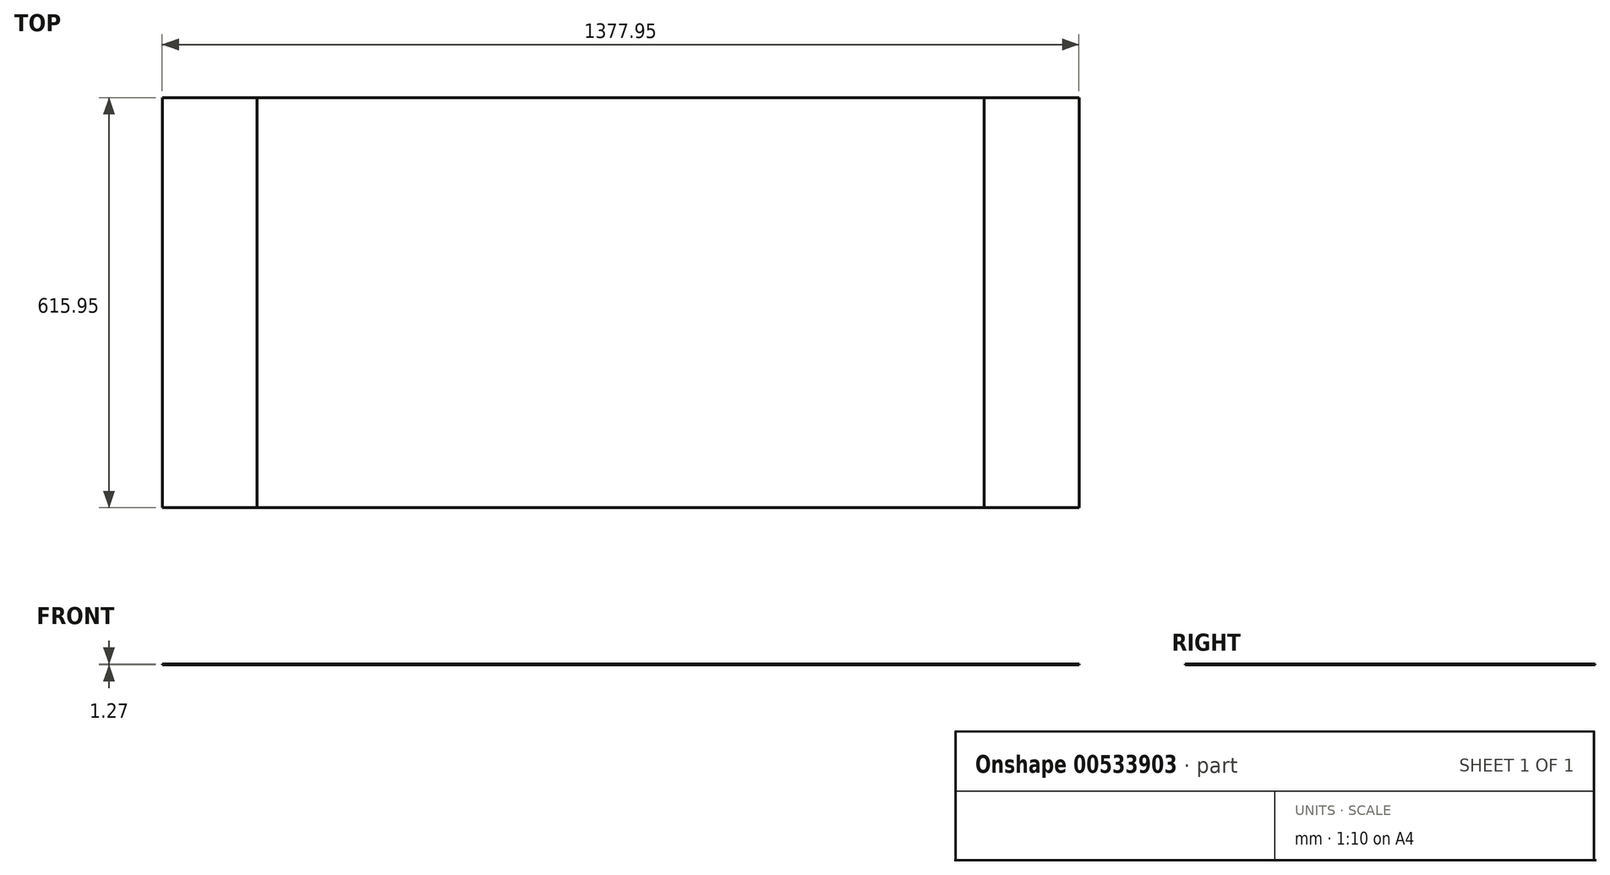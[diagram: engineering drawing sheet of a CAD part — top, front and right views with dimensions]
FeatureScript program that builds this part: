
annotation { "Feature Type Name" : "Feature", "Feature Type Description" : "" }
export const myFeature = defineFeature(function(context is Context, id is Id, definition is map)
    precondition{}
    {
        {
            var Q0;
            Q0=qCreatedBy(makeId("Top.planeOp"),FACE);
            var sketch = newSketch(context, id + "F0", { "sketchPlane" : qUnion([Q0])});
            skLineSegment(sketch, "E0", {"start": v(-107.2, 108.98) * mm, "end": v(-107.2, -506.97) * mm});
            skLineSegment(sketch, "E1", {"start": v(-107.2, -506.97) * mm, "end": v(1270.75, -506.97) * mm});
            skLineSegment(sketch, "E2", {"start": v(1270.75, -506.97) * mm, "end": v(1270.75, 108.98) * mm});
            skLineSegment(sketch, "E3", {"start": v(-107.2, 108.98) * mm, "end": v(1270.75, 108.98) * mm});
            skSolve(sketch);
        }
        {
            var Q0;
            Q0 = qSketchRegion(id + "F0", true);
            extrude(context, id + "F1", {"entities" : qUnion([Q0]), "depth" : 1.27 * mm, "offsetDistance" : 25.4 * mm});
        }
        {
            var Q0;
            Q0=makeQuery(id+"F1.opExtrude","CAP_FACE",FACE,{"disambiguationData":[OSD([sQuery(id+"F0.wireOp",EDGE,"E0"),sQuery(id+"F0.wireOp",EDGE,"E1"),sQuery(id+"F0.wireOp",EDGE,"E2"),sQuery(id+"F0.wireOp",EDGE,"E3")])],"isStart":false});
            var sketch = newSketch(context, id + "F2", { "sketchPlane" : qUnion([Q0])});
            skLineSegment(sketch, "E4.bottom", {"start": v(-107.2, -506.97) * mm, "end": v(35.2, -506.97) * mm});
            skLineSegment(sketch, "E4.top", {"start": v(-107.2, 108.98) * mm, "end": v(35.2, 108.98) * mm});
            skLineSegment(sketch, "E4.left", {"start": v(-107.2, -506.97) * mm, "end": v(-107.2, 108.98) * mm});
            skLineSegment(sketch, "E4.right", {"start": v(35.2, -506.97) * mm, "end": v(35.2, 108.98) * mm});
            skLineSegment(sketch, "E5", {"start": v(581.78, 108.98) * mm, "end": v(581.78, -506.97) * mm});
            skLineSegment(sketch, "E6.MirrorCS", {"start": v(1270.75, 108.98) * mm, "end": v(1128.36, 108.98) * mm});
            skLineSegment(sketch, "E7.MirrorCS", {"start": v(1270.75, -506.97) * mm, "end": v(1128.36, -506.97) * mm});
            skLineSegment(sketch, "E8.MirrorCS", {"start": v(1270.75, -506.97) * mm, "end": v(1270.75, 108.98) * mm});
            skLineSegment(sketch, "E9.MirrorCS", {"start": v(1128.36, -506.97) * mm, "end": v(1128.36, 108.98) * mm});
            skSolve(sketch);
        }
        {
            var Q0;
            Q0 = qSketchRegion(id + "F2", true);
            extrude(context, id + "F3", {"entities" : qUnion([Q0]), "depth" : 0 * mm, "offsetDistance" : 25.4 * mm});
        }
    });
